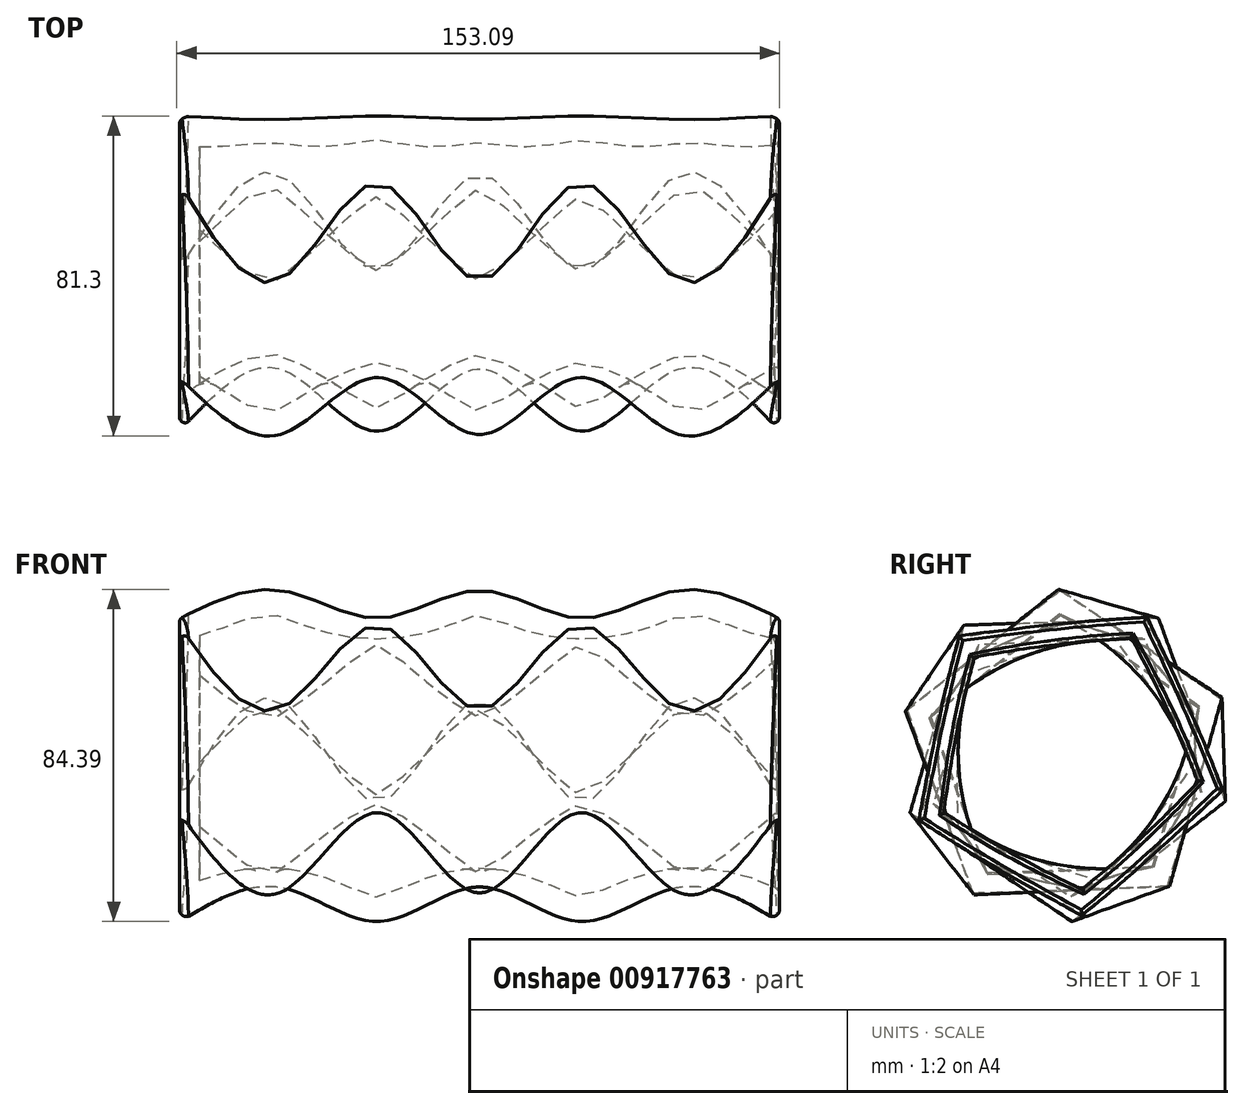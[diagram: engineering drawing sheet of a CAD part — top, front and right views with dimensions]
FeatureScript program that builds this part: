
annotation { "Feature Type Name" : "Feature", "Feature Type Description" : "" }
export const myFeature = defineFeature(function(context is Context, id is Id, definition is map)
    precondition{}
    {
        {
            var Q0;
            Q0=qCreatedBy(makeId("Right.planeOp"),FACE);
            var sketch = newSketch(context, id + "F0", { "sketchPlane" : qUnion([Q0])});
            skCircle(sketch, "E0.cCircle", {"center": v(0, 0) * mm, "radius": 34.08 * mm, "construction": true});
            skLineSegment(sketch, "E0.0", {"start": v(23.5, 34.95) * mm, "end": v(40.5, -11.56) * mm});
            skLineSegment(sketch, "E0.1", {"start": v(40.5, -11.56) * mm, "end": v(1.53, -42.1) * mm});
            skLineSegment(sketch, "E0.2", {"start": v(1.53, -42.1) * mm, "end": v(-39.56, -14.46) * mm});
            skLineSegment(sketch, "E0.3", {"start": v(-39.56, -14.46) * mm, "end": v(-25.98, 33.16) * mm});
            skLineSegment(sketch, "E0.4", {"start": v(-25.98, 33.16) * mm, "end": v(23.5, 34.95) * mm});
            skPoint(sketch, "E0.0.midPoint", {"position": v(32, 11.7) * mm});
            skSolve(sketch);
        }
        {
            var Q0;
            Q0=makeQuery(id+"F0.imprint","IMPRINT",FACE,{"disambiguationData":[TD([[makeQuery(id+"F0.imprint","IMPRINT",EDGE,{"derivedFrom":sQuery(id+"F0.wireOp",EDGE,"E0.0")}),-1.0]])]});
            cPlane(context, id + "F1", {"entities" : qUnion([Q0]), "cplaneType" : CPlaneType.OFFSET, "offset" : 25.4 * mm, "width" : 152.4 * mm, "height" : 152.4 * mm});
        }
        {
            var Q0;
            Q0=qCreatedBy(id+"F1.planeOp",FACE);
            var sketch = newSketch(context, id + "F2", { "sketchPlane" : qUnion([Q0])});
            skCircle(sketch, "E1.cCircle", {"center": v(0, 0) * mm, "radius": 34.08 * mm, "construction": true});
            skLineSegment(sketch, "E1.0", {"start": v(-1.25, 42.1) * mm, "end": v(39.66, 14.2) * mm});
            skLineSegment(sketch, "E1.1", {"start": v(39.66, 14.2) * mm, "end": v(25.76, -33.33) * mm});
            skLineSegment(sketch, "E1.2", {"start": v(25.76, -33.33) * mm, "end": v(-23.74, -34.8) * mm});
            skLineSegment(sketch, "E1.3", {"start": v(-23.74, -34.8) * mm, "end": v(-40.43, 11.82) * mm});
            skLineSegment(sketch, "E1.4", {"start": v(-40.43, 11.82) * mm, "end": v(-1.25, 42.1) * mm});
            skPoint(sketch, "E1.0.midPoint", {"position": v(19.2, 28.15) * mm});
            skSolve(sketch);
        }
        {
            var Q0;
            Q0=qCreatedBy(id+"F1.planeOp",FACE);
            cPlane(context, id + "F3", {"entities" : qUnion([Q0]), "cplaneType" : CPlaneType.OFFSET, "offset" : 25.4 * mm, "width" : 152.4 * mm, "height" : 152.4 * mm});
        }
        {
            var Q0;
            Q0=qCreatedBy(id+"F3.planeOp",FACE);
            var sketch = newSketch(context, id + "F4", { "sketchPlane" : qUnion([Q0])});
            skCircle(sketch, "E2.cCircle", {"center": v(0, 0) * mm, "radius": 34.08 * mm, "construction": true});
            skLineSegment(sketch, "E2.0", {"start": v(23.5, 34.95) * mm, "end": v(40.5, -11.56) * mm});
            skLineSegment(sketch, "E2.1", {"start": v(40.5, -11.56) * mm, "end": v(1.53, -42.1) * mm});
            skLineSegment(sketch, "E2.2", {"start": v(1.53, -42.1) * mm, "end": v(-39.56, -14.46) * mm});
            skLineSegment(sketch, "E2.3", {"start": v(-39.56, -14.46) * mm, "end": v(-25.98, 33.16) * mm});
            skLineSegment(sketch, "E2.4", {"start": v(-25.98, 33.16) * mm, "end": v(23.5, 34.95) * mm});
            skPoint(sketch, "E2.0.midPoint", {"position": v(32, 11.7) * mm});
            skSolve(sketch);
        }
        {
            var Q0;
            Q0=makeQuery(id+"F4.imprint","IMPRINT",FACE,{"disambiguationData":[TD([[makeQuery(id+"F4.imprint","IMPRINT",EDGE,{"derivedFrom":sQuery(id+"F4.wireOp",EDGE,"E2.0")}),-1.0]])]});
            cPlane(context, id + "F5", {"entities" : qUnion([Q0]), "cplaneType" : CPlaneType.OFFSET, "offset" : 25.4 * mm, "width" : 152.4 * mm, "height" : 152.4 * mm});
        }
        {
            var Q0;
            Q0=qCreatedBy(id+"F5.planeOp",FACE);
            var sketch = newSketch(context, id + "F6", { "sketchPlane" : qUnion([Q0])});
            skCircle(sketch, "E3.cCircle", {"center": v(0, 0) * mm, "radius": 34.08 * mm, "construction": true});
            skLineSegment(sketch, "E3.0", {"start": v(-1.25, 42.1) * mm, "end": v(39.66, 14.2) * mm});
            skLineSegment(sketch, "E3.1", {"start": v(39.66, 14.2) * mm, "end": v(25.76, -33.33) * mm});
            skLineSegment(sketch, "E3.2", {"start": v(25.76, -33.33) * mm, "end": v(-23.74, -34.8) * mm});
            skLineSegment(sketch, "E3.3", {"start": v(-23.74, -34.8) * mm, "end": v(-40.43, 11.82) * mm});
            skLineSegment(sketch, "E3.4", {"start": v(-40.43, 11.82) * mm, "end": v(-1.25, 42.1) * mm});
            skPoint(sketch, "E3.0.midPoint", {"position": v(19.2, 28.15) * mm});
            skSolve(sketch);
        }
        {
            var Q0;
            Q0=makeQuery(id+"F6.imprint","IMPRINT",FACE,{"disambiguationData":[TD([[makeQuery(id+"F6.imprint","IMPRINT",EDGE,{"derivedFrom":sQuery(id+"F6.wireOp",EDGE,"E3.0")}),-1.0]])]});
            cPlane(context, id + "F7", {"entities" : qUnion([Q0]), "cplaneType" : CPlaneType.OFFSET, "offset" : 25.4 * mm, "width" : 152.4 * mm, "height" : 152.4 * mm});
        }
        {
            var Q0;
            Q0=qCreatedBy(id+"F7.planeOp",FACE);
            var sketch = newSketch(context, id + "F8", { "sketchPlane" : qUnion([Q0])});
            skCircle(sketch, "E4.cCircle", {"center": v(0, 0) * mm, "radius": 34.08 * mm, "construction": true});
            skLineSegment(sketch, "E4.0", {"start": v(23.5, 34.95) * mm, "end": v(40.5, -11.56) * mm});
            skLineSegment(sketch, "E4.1", {"start": v(40.5, -11.56) * mm, "end": v(1.53, -42.1) * mm});
            skLineSegment(sketch, "E4.2", {"start": v(1.53, -42.1) * mm, "end": v(-39.56, -14.46) * mm});
            skLineSegment(sketch, "E4.3", {"start": v(-39.56, -14.46) * mm, "end": v(-25.98, 33.16) * mm});
            skLineSegment(sketch, "E4.4", {"start": v(-25.98, 33.16) * mm, "end": v(23.5, 34.95) * mm});
            skPoint(sketch, "E4.0.midPoint", {"position": v(32, 11.7) * mm});
            skSolve(sketch);
        }
        {
            var Q0;
            Q0=makeQuery(id+"F8.imprint","IMPRINT",FACE,{"disambiguationData":[TD([[makeQuery(id+"F8.imprint","IMPRINT",EDGE,{"derivedFrom":sQuery(id+"F8.wireOp",EDGE,"E4.0")}),-1.0]])]});
            cPlane(context, id + "F9", {"entities" : qUnion([Q0]), "cplaneType" : CPlaneType.OFFSET, "offset" : 25.4 * mm, "width" : 152.4 * mm, "height" : 152.4 * mm});
        }
        {
            var Q0;
            Q0=qCreatedBy(id+"F9.planeOp",FACE);
            var sketch = newSketch(context, id + "F10", { "sketchPlane" : qUnion([Q0])});
            skCircle(sketch, "E5.cCircle", {"center": v(0, 0) * mm, "radius": 34.08 * mm, "construction": true});
            skLineSegment(sketch, "E5.0", {"start": v(-1.25, 42.1) * mm, "end": v(39.66, 14.2) * mm});
            skLineSegment(sketch, "E5.1", {"start": v(39.66, 14.2) * mm, "end": v(25.76, -33.33) * mm});
            skLineSegment(sketch, "E5.2", {"start": v(25.76, -33.33) * mm, "end": v(-23.74, -34.8) * mm});
            skLineSegment(sketch, "E5.3", {"start": v(-23.74, -34.8) * mm, "end": v(-40.43, 11.82) * mm});
            skLineSegment(sketch, "E5.4", {"start": v(-40.43, 11.82) * mm, "end": v(-1.25, 42.1) * mm});
            skPoint(sketch, "E5.0.midPoint", {"position": v(19.2, 28.15) * mm});
            skSolve(sketch);
        }
        {
            var Q0;
            Q0=makeQuery(id+"F10.imprint","IMPRINT",FACE,{"disambiguationData":[TD([[makeQuery(id+"F10.imprint","IMPRINT",EDGE,{"derivedFrom":sQuery(id+"F10.wireOp",EDGE,"E5.0")}),-1.0]])]});
            cPlane(context, id + "F11", {"entities" : qUnion([Q0]), "cplaneType" : CPlaneType.OFFSET, "offset" : 25.4 * mm, "width" : 152.4 * mm, "height" : 152.4 * mm});
        }
        {
            var Q0;
            Q0=qCreatedBy(id+"F11.planeOp",FACE);
            var sketch = newSketch(context, id + "F12", { "sketchPlane" : qUnion([Q0])});
            skCircle(sketch, "E6.cCircle", {"center": v(0, 0) * mm, "radius": 34.08 * mm, "construction": true});
            skLineSegment(sketch, "E6.0", {"start": v(23.5, 34.95) * mm, "end": v(40.5, -11.56) * mm});
            skLineSegment(sketch, "E6.1", {"start": v(40.5, -11.56) * mm, "end": v(1.53, -42.1) * mm});
            skLineSegment(sketch, "E6.2", {"start": v(1.53, -42.1) * mm, "end": v(-39.56, -14.46) * mm});
            skLineSegment(sketch, "E6.3", {"start": v(-39.56, -14.46) * mm, "end": v(-25.98, 33.16) * mm});
            skLineSegment(sketch, "E6.4", {"start": v(-25.98, 33.16) * mm, "end": v(23.5, 34.95) * mm});
            skPoint(sketch, "E6.0.midPoint", {"position": v(32, 11.7) * mm});
            skSolve(sketch);
        }
        {
            var Q0;
            Q0=qCreatedBy(id+"F11.planeOp",FACE);
            cPlane(context, id + "F13", {"entities" : qUnion([Q0]), "cplaneType" : CPlaneType.OFFSET, "offset" : 25.4 * mm, "width" : 152.4 * mm, "height" : 152.4 * mm});
        }
        {
            var Q0;
            Q0=makeQuery(id+"F0.imprint","IMPRINT",FACE,{"disambiguationData":[TD([[makeQuery(id+"F0.imprint","IMPRINT",EDGE,{"derivedFrom":sQuery(id+"F0.wireOp",EDGE,"E0.0")}),-1.0]])]});
            var Q1;
            Q1=makeQuery(id+"F2.imprint","IMPRINT",FACE,{"disambiguationData":[TD([[makeQuery(id+"F2.imprint","IMPRINT",EDGE,{"derivedFrom":sQuery(id+"F2.wireOp",EDGE,"E1.0")}),-1.0]])]});
            var Q2;
            Q2=makeQuery(id+"F4.imprint","IMPRINT",FACE,{"disambiguationData":[TD([[makeQuery(id+"F4.imprint","IMPRINT",EDGE,{"derivedFrom":sQuery(id+"F4.wireOp",EDGE,"E2.0")}),-1.0]])]});
            var Q3;
            Q3=makeQuery(id+"F6.imprint","IMPRINT",FACE,{"disambiguationData":[TD([[makeQuery(id+"F6.imprint","IMPRINT",EDGE,{"derivedFrom":sQuery(id+"F6.wireOp",EDGE,"E3.0")}),-1.0]])]});
            var Q4;
            Q4=makeQuery(id+"F8.imprint","IMPRINT",FACE,{"disambiguationData":[TD([[makeQuery(id+"F8.imprint","IMPRINT",EDGE,{"derivedFrom":sQuery(id+"F8.wireOp",EDGE,"E4.0")}),-1.0]])]});
            var Q5;
            Q5=makeQuery(id+"F10.imprint","IMPRINT",FACE,{"disambiguationData":[TD([[makeQuery(id+"F10.imprint","IMPRINT",EDGE,{"derivedFrom":sQuery(id+"F10.wireOp",EDGE,"E5.0")}),-1.0]])]});
            var Q6;
            Q6=makeQuery(id+"F12.imprint","IMPRINT",FACE,{"disambiguationData":[TD([[makeQuery(id+"F12.imprint","IMPRINT",EDGE,{"derivedFrom":sQuery(id+"F12.wireOp",EDGE,"E6.0")}),-1.0]])]});
            loft(context, id + "F14", {"sheetProfilesArray" : [{ "sheetProfileEntities" : qUnion([Q0]) }, { "sheetProfileEntities" : qUnion([Q1]) }, { "sheetProfileEntities" : qUnion([Q2]) }, { "sheetProfileEntities" : qUnion([Q3]) }, { "sheetProfileEntities" : qUnion([Q4]) }, { "sheetProfileEntities" : qUnion([Q5]) }, { "sheetProfileEntities" : qUnion([Q6]) }]});
        }
        {
            var Q0;
            Q0=makeQuery(id+"F14.opLoft","CAP_FACE",FACE,{"disambiguationData":[OSD([makeQuery(id+"F12.imprint","IMPRINT",FACE,{"disambiguationData":[TD([[makeQuery(id+"F12.imprint","IMPRINT",EDGE,{"derivedFrom":sQuery(id+"F12.wireOp",EDGE,"E6.0")}),-1.0]])]})])],"isStart":true});
            shell(context, id + "F15", {"entities" : qUnion([Q0]), "thickness" : 5.08 * mm});
        }
        {
            var Q0;
            Q0=makeQuery(id+"F14.opLoft","MID_CAP_EDGE",EDGE,{"disambiguationData":[OSD([sQuery(id+"F12.wireOp",EDGE,"E6.1"),sQuery(id+"F12.wireOp",EDGE,"E6.2"),sQuery(id+"F12.wireOp",EDGE,"E6.3")])],"capPos":6.0});
            var Q1;
            Q1=makeQuery(id+"F14.opLoft","MID_CAP_EDGE",EDGE,{"disambiguationData":[OSD([sQuery(id+"F12.wireOp",EDGE,"E6.0"),sQuery(id+"F12.wireOp",EDGE,"E6.1"),sQuery(id+"F12.wireOp",EDGE,"E6.2")])],"capPos":6.0});
            var Q2;
            Q2=makeQuery(id+"F14.opLoft","MID_CAP_EDGE",EDGE,{"disambiguationData":[OSD([sQuery(id+"F12.wireOp",EDGE,"E6.0"),sQuery(id+"F12.wireOp",EDGE,"E6.1"),sQuery(id+"F12.wireOp",EDGE,"E6.4")])],"capPos":6.0});
            var Q3;
            Q3=makeQuery(id+"F14.opLoft","MID_CAP_EDGE",EDGE,{"disambiguationData":[OSD([sQuery(id+"F12.wireOp",EDGE,"E6.0"),sQuery(id+"F12.wireOp",EDGE,"E6.3"),sQuery(id+"F12.wireOp",EDGE,"E6.4")])],"capPos":6.0});
            var Q4;
            Q4=makeQuery(id+"F14.opLoft","MID_CAP_EDGE",EDGE,{"disambiguationData":[OSD([sQuery(id+"F12.wireOp",EDGE,"E6.2"),sQuery(id+"F12.wireOp",EDGE,"E6.3"),sQuery(id+"F12.wireOp",EDGE,"E6.4")])],"capPos":6.0});
            var Q5;
            Q5=makeQuery(id+"F15.opShell","OFFSET_EDGE",EDGE,{"disambiguationData":[OSD([sQuery(id+"F12.wireOp",EDGE,"E6.0"),sQuery(id+"F12.wireOp",EDGE,"E6.3"),sQuery(id+"F12.wireOp",EDGE,"E6.4")])]});
            var Q6;
            Q6=makeQuery(id+"F15.opShell","OFFSET_EDGE",EDGE,{"disambiguationData":[OSD([sQuery(id+"F12.wireOp",EDGE,"E6.0"),sQuery(id+"F12.wireOp",EDGE,"E6.1"),sQuery(id+"F12.wireOp",EDGE,"E6.4")])]});
            var Q7;
            Q7=makeQuery(id+"F15.opShell","OFFSET_EDGE",EDGE,{"disambiguationData":[OSD([sQuery(id+"F12.wireOp",EDGE,"E6.0"),sQuery(id+"F12.wireOp",EDGE,"E6.1"),sQuery(id+"F12.wireOp",EDGE,"E6.2")])]});
            var Q8;
            Q8=makeQuery(id+"F15.opShell","OFFSET_EDGE",EDGE,{"disambiguationData":[OSD([sQuery(id+"F12.wireOp",EDGE,"E6.1"),sQuery(id+"F12.wireOp",EDGE,"E6.2"),sQuery(id+"F12.wireOp",EDGE,"E6.3")])]});
            var Q9;
            Q9=makeQuery(id+"F15.opShell","OFFSET_EDGE",EDGE,{"disambiguationData":[OSD([sQuery(id+"F12.wireOp",EDGE,"E6.2"),sQuery(id+"F12.wireOp",EDGE,"E6.3"),sQuery(id+"F12.wireOp",EDGE,"E6.4")])]});
            fillet(context, id + "F16", {"entities" : qUnion([Q0, Q1, Q2, Q3, Q4, Q5, Q6, Q7, Q8, Q9]), "radius" : 1.27 * mm, "tangentPropagation" : true, "allowEdgeOverflow" : false});
        }
        {
            var Q0;
            Q0=makeQuery(id+"F14.opLoft","MID_CAP_EDGE",EDGE,{"disambiguationData":[OSD([sQuery(id+"F0.wireOp",EDGE,"E0.0"),sQuery(id+"F0.wireOp",EDGE,"E0.1"),sQuery(id+"F0.wireOp",EDGE,"E0.4")])],"capPos":0.0});
            var Q1;
            Q1=makeQuery(id+"F14.opLoft","MID_CAP_EDGE",EDGE,{"disambiguationData":[OSD([sQuery(id+"F0.wireOp",EDGE,"E0.0"),sQuery(id+"F0.wireOp",EDGE,"E0.3"),sQuery(id+"F0.wireOp",EDGE,"E0.4")])],"capPos":0.0});
            var Q2;
            Q2=makeQuery(id+"F14.opLoft","MID_CAP_EDGE",EDGE,{"disambiguationData":[OSD([sQuery(id+"F0.wireOp",EDGE,"E0.2"),sQuery(id+"F0.wireOp",EDGE,"E0.3"),sQuery(id+"F0.wireOp",EDGE,"E0.4")])],"capPos":0.0});
            var Q3;
            Q3=makeQuery(id+"F14.opLoft","MID_CAP_EDGE",EDGE,{"disambiguationData":[OSD([sQuery(id+"F0.wireOp",EDGE,"E0.1"),sQuery(id+"F0.wireOp",EDGE,"E0.2"),sQuery(id+"F0.wireOp",EDGE,"E0.3")])],"capPos":0.0});
            var Q4;
            Q4=makeQuery(id+"F14.opLoft","MID_CAP_EDGE",EDGE,{"disambiguationData":[OSD([sQuery(id+"F0.wireOp",EDGE,"E0.0"),sQuery(id+"F0.wireOp",EDGE,"E0.1"),sQuery(id+"F0.wireOp",EDGE,"E0.2")])],"capPos":0.0});
            fillet(context, id + "F17", {"entities" : qUnion([Q0, Q1, Q2, Q3, Q4]), "radius" : 1.27 * mm, "tangentPropagation" : true, "allowEdgeOverflow" : false});
        }
    });
